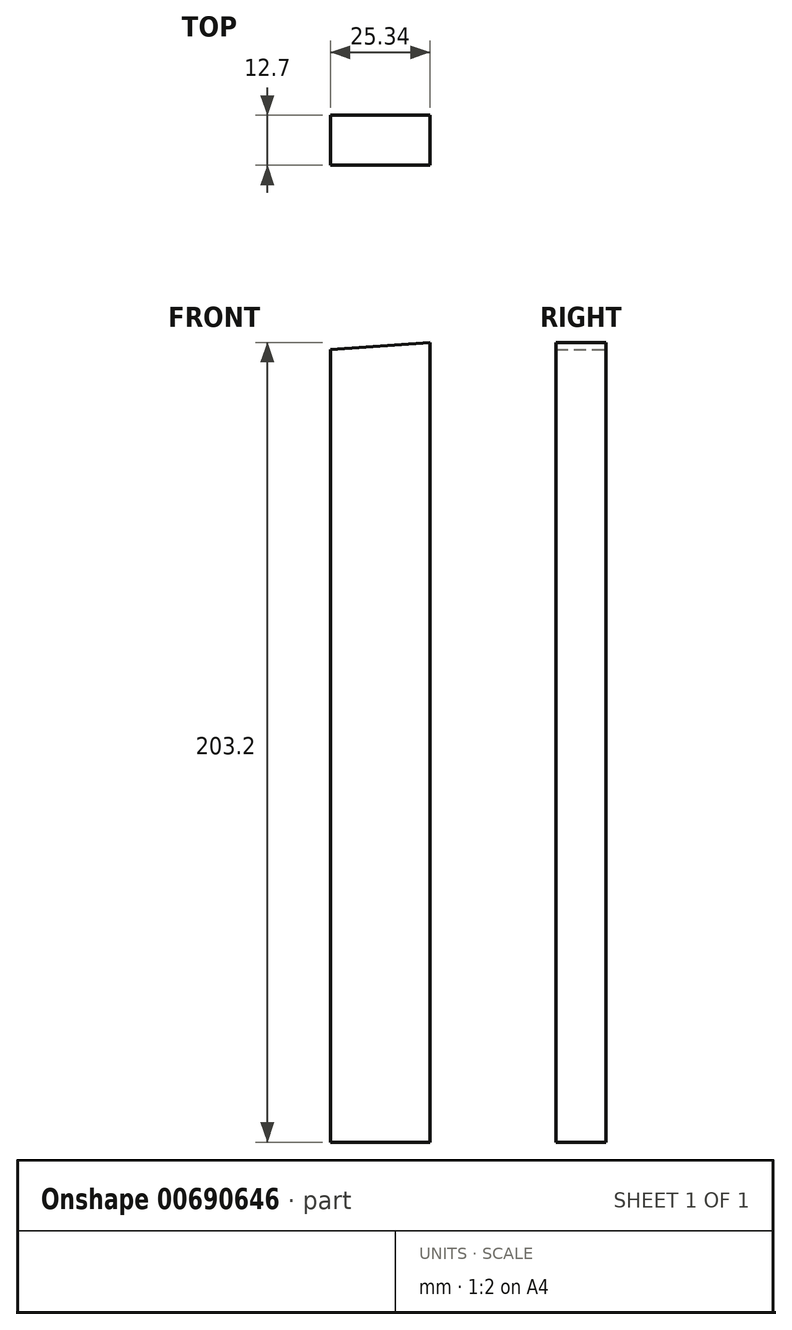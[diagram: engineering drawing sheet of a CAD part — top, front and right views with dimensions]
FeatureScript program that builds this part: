
annotation { "Feature Type Name" : "Feature", "Feature Type Description" : "" }
export const myFeature = defineFeature(function(context is Context, id is Id, definition is map)
    precondition{}
    {
        {
            var Q0;
            Q0=qCreatedBy(makeId("Front.planeOp"),FACE);
            var sketch = newSketch(context, id + "F0", { "sketchPlane" : qUnion([Q0])});
            skLineSegment(sketch, "E0", {"start": v(-50.58, 89.73) * mm, "end": v(-50.58, -111.71) * mm});
            skLineSegment(sketch, "E1", {"start": v(-25.24, -111.71) * mm, "end": v(-25.24, 91.49) * mm});
            skLineSegment(sketch, "E2", {"start": v(-25.24, 91.49) * mm, "end": v(-50.58, 89.73) * mm});
            skLineSegment(sketch, "E3", {"start": v(-25.24, -111.71) * mm, "end": v(-50.58, -111.71) * mm});
            skSolve(sketch);
        }
        {
            var Q0;
            Q0=makeQuery(id+"F0.imprint","IMPRINT",FACE,{"disambiguationData":[TD([[makeQuery(id+"F0.imprint","IMPRINT",EDGE,{"derivedFrom":sQuery(id+"F0.wireOp",EDGE,"E0")}),1.0]])]});
            extrude(context, id + "F1", {"entities" : qUnion([Q0]), "depth" : 12.7 * mm, "offsetDistance" : 25.4 * mm});
        }
    });
